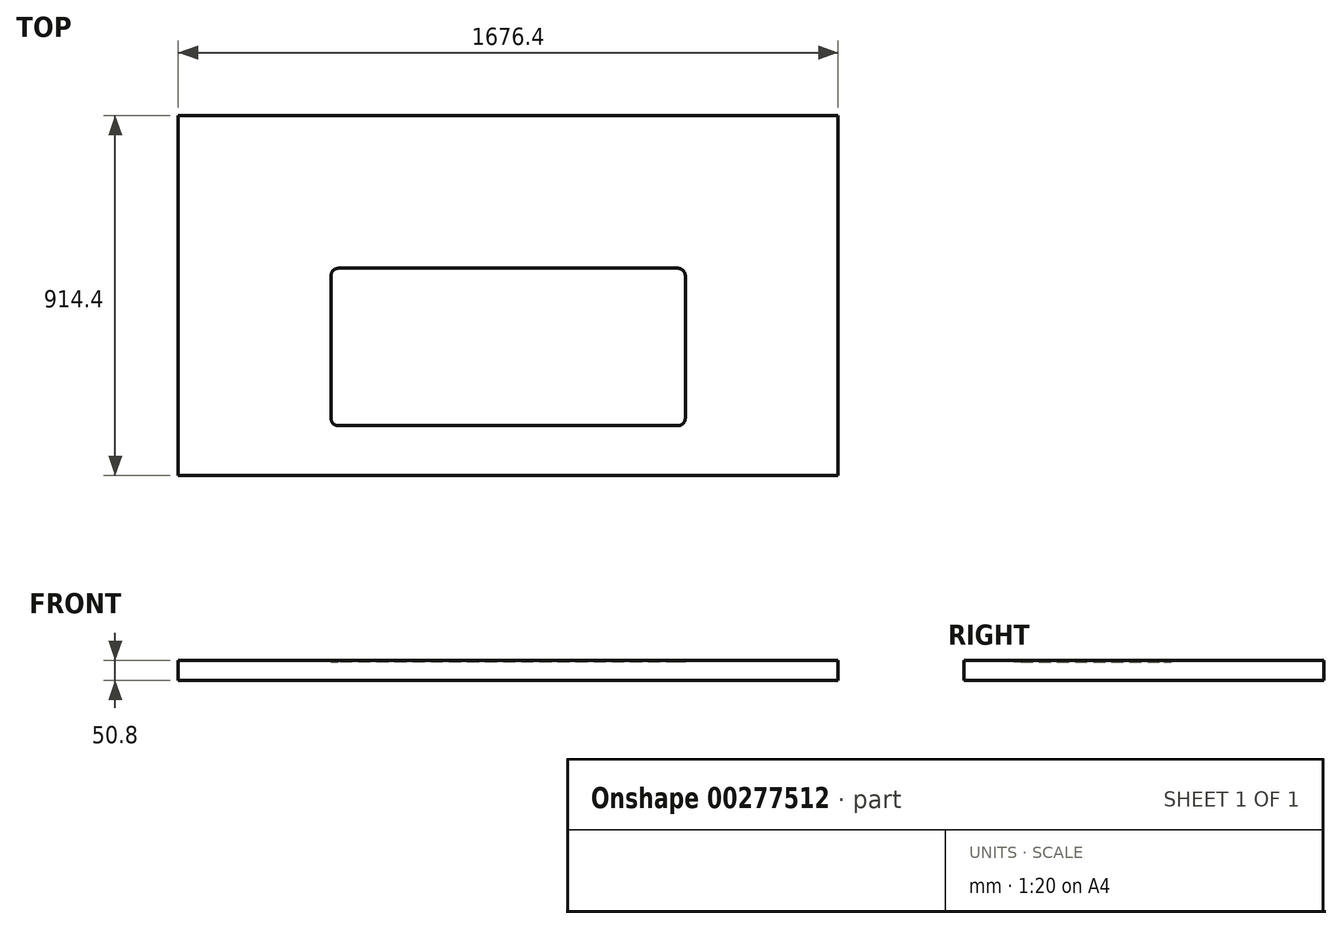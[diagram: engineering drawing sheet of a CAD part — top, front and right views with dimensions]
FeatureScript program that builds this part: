
annotation { "Feature Type Name" : "Feature", "Feature Type Description" : "" }
export const myFeature = defineFeature(function(context is Context, id is Id, definition is map)
    precondition{}
    {
        {
            var Q0;
            Q0=qCreatedBy(makeId("Top.planeOp"),FACE);
            var sketch = newSketch(context, id + "F0", { "sketchPlane" : qUnion([Q0])});
            skLineSegment(sketch, "E0.bottom", {"start": v(-838.2, 457.2) * mm, "end": v(838.2, 457.2) * mm});
            skLineSegment(sketch, "E0.top", {"start": v(-838.2, -457.2) * mm, "end": v(838.2, -457.2) * mm});
            skLineSegment(sketch, "E0.left", {"start": v(-838.2, 457.2) * mm, "end": v(-838.2, -457.2) * mm});
            skLineSegment(sketch, "E0.right", {"start": v(838.2, 457.2) * mm, "end": v(838.2, -457.2) * mm});
            skPoint(sketch, "E0.middle", {"position": v(0, 0) * mm});
            skSolve(sketch);
        }
        {
            var Q0;
            Q0=makeQuery(id+"F0.imprint","IMPRINT",FACE,{"disambiguationData":[TD([[makeQuery(id+"F0.imprint","IMPRINT",EDGE,{"derivedFrom":sQuery(id+"F0.wireOp",EDGE,"E0.bottom")}),-1.0]])]});
            extrude(context, id + "F1", {"entities" : qUnion([Q0]), "depth" : 50.8 * mm});
        }
        {
            var Q0;
            Q0=makeQuery(id+"F1.opExtrude","CAP_FACE",FACE,{"disambiguationData":[OSD([sQuery(id+"F0.wireOp",EDGE,"E0.bottom"),sQuery(id+"F0.wireOp",EDGE,"E0.top"),sQuery(id+"F0.wireOp",EDGE,"E0.left"),sQuery(id+"F0.wireOp",EDGE,"E0.right")])],"isStart":false});
            var sketch = newSketch(context, id + "F2", { "sketchPlane" : qUnion([Q0])});
            skLineSegment(sketch, "E1.bottom", {"start": v(431.74, -330.91) * mm, "end": v(-431.74, -330.91) * mm});
            skLineSegment(sketch, "E1.top", {"start": v(431.74, 69.09) * mm, "end": v(-431.73, 69.09) * mm});
            skLineSegment(sketch, "E1.left", {"start": v(450, -312.65) * mm, "end": v(450, 50.83) * mm});
            skLineSegment(sketch, "E1.right", {"start": v(-450, -312.65) * mm, "end": v(-450, 50.82) * mm});
            skPoint(sketch, "E1.middle", {"position": v(0, -130.91) * mm});
            skPoint(sketch, "E2.visualSharp", {"position": v(-450, 69.09) * mm});
            skArc(sketch, "E2.filletArc", {"start": v(-431.73, 69.09) * mm, "mid": v(-444.65, 63.74) * mm, "end": v(-450, 50.82) * mm});
            skPoint(sketch, "E3.visualSharp", {"position": v(450, 69.09) * mm});
            skArc(sketch, "E3.filletArc", {"start": v(450, 50.83) * mm, "mid": v(444.65, 63.74) * mm, "end": v(431.74, 69.09) * mm});
            skPoint(sketch, "E4.visualSharp", {"position": v(450, -330.91) * mm});
            skArc(sketch, "E4.filletArc", {"start": v(431.74, -330.91) * mm, "mid": v(444.65, -325.56) * mm, "end": v(450, -312.65) * mm});
            skPoint(sketch, "E5.visualSharp", {"position": v(-450, -330.91) * mm});
            skArc(sketch, "E5.filletArc", {"start": v(-450, -312.65) * mm, "mid": v(-444.65, -325.56) * mm, "end": v(-431.74, -330.91) * mm});
            skSolve(sketch);
        }
        {
            var Q0;
            Q0=makeQuery(id+"F2.imprint","IMPRINT",FACE,{"disambiguationData":[TD([[makeQuery(id+"F2.imprint","IMPRINT",EDGE,{"derivedFrom":sQuery(id+"F2.wireOp",EDGE,"E1.bottom")}),-1.0]])]});
            extrude(context, id + "F3", {"entities" : qUnion([Q0]), "operationType" : NewBodyOperationType.REMOVE, "oppositeDirection" : true, "depth" : 4 * mm});
        }
    });
